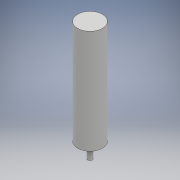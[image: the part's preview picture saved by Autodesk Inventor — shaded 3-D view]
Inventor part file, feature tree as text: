
AUTODESK INVENTOR PART (.ipt)
format: ipt  version: 2017 SP1 (Build 210196100, 196)  size: 115,200 bytes
history: native  units: mm
features: extrude x4, sketch x4
ambient origin geometry x8: Origin, YZ Plane, XZ Plane, XY Plane, X Axis, Y Axis, Z Axis, Center Point
bodies: Solide1 (feature_tree)
feature tree (8):
  extrude  "Extrusion1"  Depth=26.0mm
  extrude  "Extrusion2"  Depth=110.0mm TaperAngle=0.0deg
  extrude  "Extrusion3"  Depth=14.0mm
  extrude  "Extrusion4"  Depth=2.0mm
  sketch  "Esquisse1"
  sketch  "Esquisse2"
  sketch  "Esquisse3"
  sketch  "Esquisse4"
